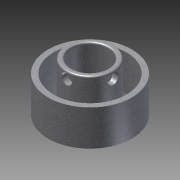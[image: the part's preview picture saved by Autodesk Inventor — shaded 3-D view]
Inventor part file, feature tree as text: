
AUTODESK INVENTOR PART (.ipt)
format: ipt  version: 2012 (Build 160160000, 160)  size: 158,720 bytes
history: native  units: mm
features: extrude x4, sketch x3, fillet x1
ambient origin geometry x8: Origin, YZ Plane, XZ Plane, XY Plane, X Axis, Y Axis, Z Axis, Center Point
bodies: Solid1 (feature_tree)
feature tree (8):
  sketch  "Sketch1"  dims[d0=48.0mm d1=3.0mm]
  extrude  "Extrusion1"  Depth=3.0mm
  extrude  "Extrusion2"  Depth=3.0mm
  extrude  "Extrusion3"  Depth=28.5mm TaperAngle=0.0deg
  extrude  "Extrusion4"  Depth=4.0mm
  fillet  "Fillet1"  Radius=6.0mm
  sketch  "Sketch2"  dims[d2=21.0mm d3=3.0mm]
  sketch  "Sketch3"  dims[d4=20.5mm d5=0.0mm d6=28.5mm d7=4.0mm d8=0.0mm d9=0.0mm d10=4.0mm d11=6.0mm d12=28.5mm d13=0.0mm d14=4.0mm d15=6.0mm d16=28.5mm d17=0.0mm d18=1.0mm]
